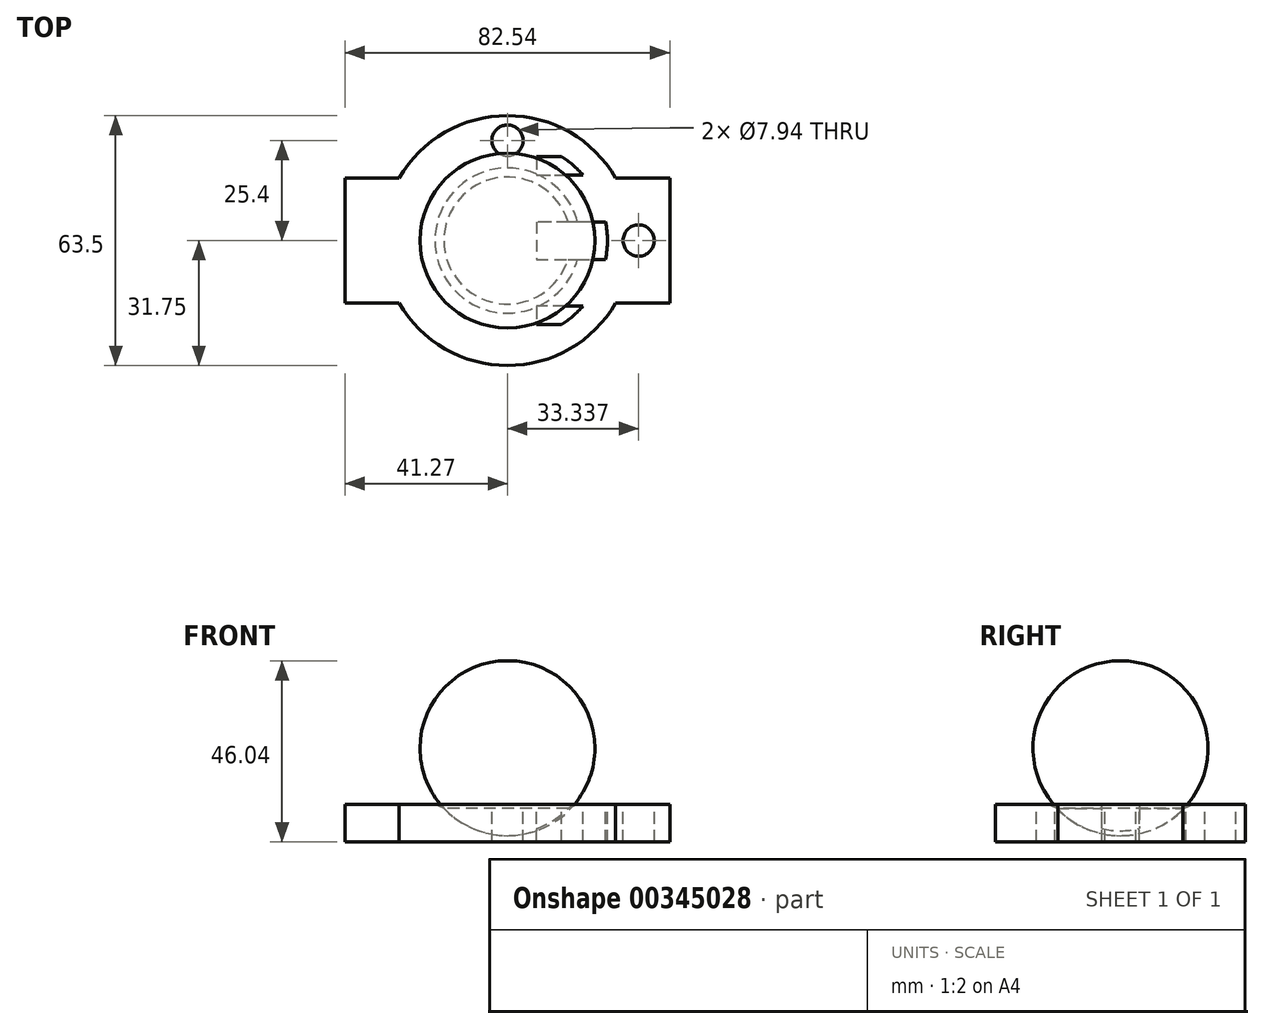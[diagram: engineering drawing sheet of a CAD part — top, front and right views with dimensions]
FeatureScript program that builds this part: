
annotation { "Feature Type Name" : "Feature", "Feature Type Description" : "" }
export const myFeature = defineFeature(function(context is Context, id is Id, definition is map)
    precondition{}
    {
        {
            var Q0;
            Q0=qCreatedBy(makeId("Top.planeOp"),FACE);
            var sketch = newSketch(context, id + "F0", { "sketchPlane" : qUnion([Q0])});
            skArc(sketch, "E0", {"start": v(-27.5, -15.87) * mm, "mid": v(0, -31.75) * mm, "end": v(27.5, -15.88) * mm});
            skLineSegment(sketch, "E1.bottom", {"start": v(-41.27, 15.88) * mm, "end": v(-27.5, 15.88) * mm});
            skLineSegment(sketch, "E1.top", {"start": v(-41.27, -15.87) * mm, "end": v(-27.5, -15.87) * mm});
            skLineSegment(sketch, "E1.left", {"start": v(-41.27, 15.88) * mm, "end": v(-41.28, -15.88) * mm});
            skLineSegment(sketch, "E1.right", {"start": v(41.28, 15.88) * mm, "end": v(41.27, -15.88) * mm});
            skLineSegment(sketch, "E2.trimOffspring", {"start": v(27.5, 15.88) * mm, "end": v(41.27, 15.87) * mm});
            skLineSegment(sketch, "E3.trimOffspring", {"start": v(27.5, -15.88) * mm, "end": v(41.27, -15.88) * mm});
            skArc(sketch, "E4.trimOffspring", {"start": v(27.5, 15.87) * mm, "mid": v(0, 31.75) * mm, "end": v(-27.5, 15.88) * mm});
            skSolve(sketch);
        }
        {
            var Q0;
            Q0=makeQuery(id+"F0.imprint","IMPRINT",FACE,{"disambiguationData":[TD([[makeQuery(id+"F0.imprint","IMPRINT",EDGE,{"derivedFrom":sQuery(id+"F0.wireOp",EDGE,"E0")}),1.0]])]});
            extrude(context, id + "F1", {"entities" : qUnion([Q0]), "depth" : 9.52 * mm});
        }
        {
            var Q0;
            Q0=makeQuery(id+"F1.opExtrude","CAP_FACE",FACE,{"disambiguationData":[OSD([sQuery(id+"F0.wireOp",EDGE,"E0"),sQuery(id+"F0.wireOp",EDGE,"E1.bottom"),sQuery(id+"F0.wireOp",EDGE,"E1.top"),sQuery(id+"F0.wireOp",EDGE,"E1.left"),sQuery(id+"F0.wireOp",EDGE,"E1.right"),sQuery(id+"F0.wireOp",EDGE,"E2.trimOffspring"),sQuery(id+"F0.wireOp",EDGE,"E3.trimOffspring"),sQuery(id+"F0.wireOp",EDGE,"E4.trimOffspring")])],"isStart":false});
            var sketch = newSketch(context, id + "F2", { "sketchPlane" : qUnion([Q0])});
            skCircle(sketch, "E5", {"center": v(0, 0) * mm, "radius": 25.4 * mm});
            skLineSegment(sketch, "E6", {"start": v(13.7, 21.39) * mm, "end": v(7.35, 21.39) * mm});
            skLineSegment(sketch, "E7", {"start": v(7.35, 21.39) * mm, "end": v(7.35, 16.63) * mm});
            skLineSegment(sketch, "E8", {"start": v(7.35, 16.63) * mm, "end": v(19.2, 16.63) * mm});
            skLineSegment(sketch, "E9", {"start": v(24.95, 4.76) * mm, "end": v(7.35, 4.76) * mm});
            skLineSegment(sketch, "E10", {"start": v(7.35, 4.76) * mm, "end": v(7.35, -4.76) * mm});
            skLineSegment(sketch, "E11", {"start": v(7.35, -4.76) * mm, "end": v(24.95, -4.76) * mm});
            skLineSegment(sketch, "E12", {"start": v(19.2, -16.63) * mm, "end": v(7.35, -16.63) * mm});
            skLineSegment(sketch, "E13", {"start": v(7.35, -16.63) * mm, "end": v(7.35, -21.39) * mm});
            skLineSegment(sketch, "E14", {"start": v(7.35, -21.39) * mm, "end": v(13.7, -21.39) * mm});
            skSolve(sketch);
        }
        {
            var Q0;
            {var subQ0=sQuery(id+"F2.wireOp",EDGE,"E6");Q0=makeQuery(id+"F2.imprint","IMPRINT",FACE,{"disambiguationData":[TD([[makeQuery(id+"F2.imprint","IMPRINT",EDGE,{"derivedFrom":subQ0}),1.0]])]});}
            var Q1;
            {var subQ0=sQuery(id+"F2.wireOp",EDGE,"E9");Q1=makeQuery(id+"F2.imprint","IMPRINT",FACE,{"disambiguationData":[TD([[makeQuery(id+"F2.imprint","IMPRINT",EDGE,{"derivedFrom":subQ0}),1.0]])]});}
            var Q2;
            {var subQ0=sQuery(id+"F2.wireOp",EDGE,"E12");Q2=makeQuery(id+"F2.imprint","IMPRINT",FACE,{"disambiguationData":[TD([[makeQuery(id+"F2.imprint","IMPRINT",EDGE,{"derivedFrom":subQ0}),1.0]])]});}
            extrude(context, id + "F3", {"entities" : qUnion([Q0, Q1, Q2]), "operationType" : NewBodyOperationType.REMOVE, "oppositeDirection" : true, "depth" : 9.52 * mm});
        }
        {
            var Q0;
            Q0=qCreatedBy(makeId("Front.planeOp"),FACE);
            var sketch = newSketch(context, id + "F4", { "sketchPlane" : qUnion([Q0])});
            skArc(sketch, "E15", {"start": v(22.23, 23.81) * mm, "mid": v(19.34, 34.76) * mm, "end": v(11.45, 42.86) * mm});
            skLineSegment(sketch, "E16", {"start": v(-22.23, 23.81) * mm, "end": v(22.23, 23.81) * mm});
            skArc(sketch, "E17.trimOffspring", {"start": v(-11.45, 42.86) * mm, "mid": v(-19.34, 34.76) * mm, "end": v(-22.23, 23.81) * mm});
            skArc(sketch, "E18", {"start": v(22.23, 23.81) * mm, "mid": v(0, 46.04) * mm, "end": v(-22.23, 23.81) * mm});
            skSolve(sketch);
        }
        {
            var Q0;
            {var subQ0=sQuery(id+"F4.wireOp",EDGE,"E16");Q0=makeQuery(id+"F4.imprint","IMPRINT",FACE,{"disambiguationData":[TD([[makeQuery(id+"F4.imprint","IMPRINT",EDGE,{"derivedFrom":subQ0}),1.0]])]});}
            var Q1;
            Q1=sQuery(id+"F4.wireOp",EDGE,"E16");
            revolve(context, id + "F5", {"operationType" : NewBodyOperationType.REMOVE, "entities" : qUnion([Q0]), "axis" : qUnion([Q1]), "revolveType" : RevolveType.FULL});
        }
        {
            var Q0;
            Q0=makeQuery(id+"F1.opExtrude","CAP_FACE",FACE,{"disambiguationData":[OSD([sQuery(id+"F0.wireOp",EDGE,"E0"),sQuery(id+"F0.wireOp",EDGE,"E1.bottom"),sQuery(id+"F0.wireOp",EDGE,"E1.top"),sQuery(id+"F0.wireOp",EDGE,"E1.left"),sQuery(id+"F0.wireOp",EDGE,"E1.right"),sQuery(id+"F0.wireOp",EDGE,"E2.trimOffspring"),sQuery(id+"F0.wireOp",EDGE,"E3.trimOffspring"),sQuery(id+"F0.wireOp",EDGE,"E4.trimOffspring")])],"isStart":false});
            var sketch = newSketch(context, id + "F6", { "sketchPlane" : qUnion([Q0])});
            skCircle(sketch, "E19", {"center": v(0, 25.4) * mm, "radius": 3.97 * mm});
            skCircle(sketch, "E20", {"center": v(33.34, 0) * mm, "radius": 3.97 * mm});
            skSolve(sketch);
        }
        {
            var Q0;
            Q0 = qSketchRegion(id + "F6", true);
            extrude(context, id + "F7", {"entities" : qUnion([Q0]), "operationType" : NewBodyOperationType.REMOVE, "endBound" : BoundingType.THROUGH_ALL, "oppositeDirection" : true, "depth" : 25.4 * mm});
        }
        {
            var Q0;
            {var subQ0=sQuery(id+"F4.wireOp",EDGE,"E16");Q0=makeQuery(id+"F4.imprint","IMPRINT",FACE,{"disambiguationData":[TD([[makeQuery(id+"F4.imprint","IMPRINT",EDGE,{"derivedFrom":subQ0}),1.0]])]});}
            var Q1;
            Q1=sQuery(id+"F4.wireOp",EDGE,"E16");
            revolve(context, id + "F8", {"entities" : qUnion([Q0]), "axis" : qUnion([Q1]), "revolveType" : RevolveType.FULL});
        }
        {
            var Q0;
            Q0=makeQuery(id+"F5.boolean.opBoolean","INTERSECT",EDGE,{"disambiguationData":[OD(0.0)],"derivedFrom":[makeQuery(id+"F1.opExtrude","CAP_FACE",FACE,{"disambiguationData":[OSD([sQuery(id+"F0.wireOp",EDGE,"E0"),sQuery(id+"F0.wireOp",EDGE,"E1.bottom"),sQuery(id+"F0.wireOp",EDGE,"E1.top"),sQuery(id+"F0.wireOp",EDGE,"E1.left"),sQuery(id+"F0.wireOp",EDGE,"E1.right"),sQuery(id+"F0.wireOp",EDGE,"E2.trimOffspring"),sQuery(id+"F0.wireOp",EDGE,"E3.trimOffspring"),sQuery(id+"F0.wireOp",EDGE,"E4.trimOffspring")])],"isStart":false}),makeQuery(id+"F5.opRevolve","SWEPT_FACE",FACE,{"disambiguationData":[OSD([sQuery(id+"F4.wireOp",EDGE,"E18")])]})]});
            var Q1;
            Q1=makeQuery(id+"F5.boolean.opBoolean","INTERSECT",EDGE,{"disambiguationData":[OD(1.0)],"derivedFrom":[makeQuery(id+"F1.opExtrude","CAP_FACE",FACE,{"disambiguationData":[OSD([sQuery(id+"F0.wireOp",EDGE,"E0"),sQuery(id+"F0.wireOp",EDGE,"E1.bottom"),sQuery(id+"F0.wireOp",EDGE,"E1.top"),sQuery(id+"F0.wireOp",EDGE,"E1.left"),sQuery(id+"F0.wireOp",EDGE,"E1.right"),sQuery(id+"F0.wireOp",EDGE,"E2.trimOffspring"),sQuery(id+"F0.wireOp",EDGE,"E3.trimOffspring"),sQuery(id+"F0.wireOp",EDGE,"E4.trimOffspring")])],"isStart":false}),makeQuery(id+"F5.opRevolve","SWEPT_FACE",FACE,{"disambiguationData":[OSD([sQuery(id+"F4.wireOp",EDGE,"E18")])]})]});
            chamfer(context, id + "F9", {"entities" : qUnion([Q0, Q1]), "width" : 3.17 * mm, "tangentPropagation" : true});
        }
    });
